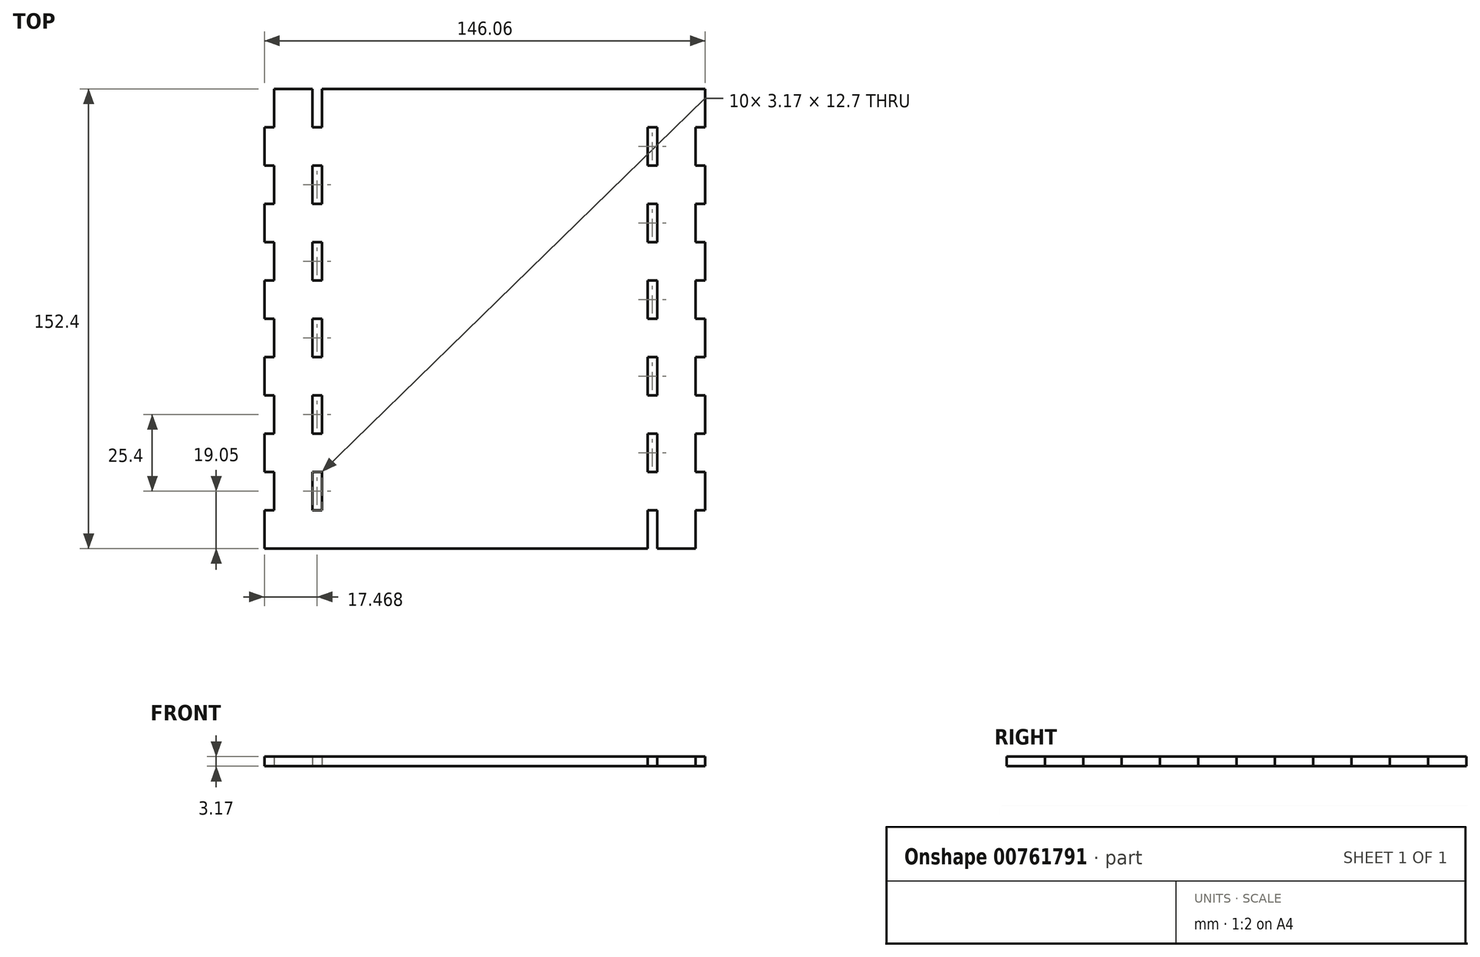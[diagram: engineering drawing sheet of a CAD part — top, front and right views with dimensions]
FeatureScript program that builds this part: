
annotation { "Feature Type Name" : "Feature", "Feature Type Description" : "" }
export const myFeature = defineFeature(function(context is Context, id is Id, definition is map)
    precondition{}
    {
        {
            var Q0;
            Q0=qCreatedBy(makeId("Top.planeOp"),FACE);
            var sketch = newSketch(context, id + "F0", { "sketchPlane" : qUnion([Q0])});
            skLineSegment(sketch, "E0.bottom", {"start": v(73.02, 76.2) * mm, "end": v(-73.03, 76.2) * mm});
            skLineSegment(sketch, "E0.top", {"start": v(73.03, -76.2) * mm, "end": v(-73.03, -76.2) * mm});
            skLineSegment(sketch, "E0.left", {"start": v(73.02, 76.2) * mm, "end": v(73.03, -76.2) * mm});
            skLineSegment(sketch, "E0.right", {"start": v(-73.03, 76.2) * mm, "end": v(-73.03, -76.2) * mm});
            skPoint(sketch, "E0.middle", {"position": v(0, 0) * mm});
            skLineSegment(sketch, "E1.bottom", {"start": v(-73.03, 76.2) * mm, "end": v(-69.85, 76.2) * mm});
            skLineSegment(sketch, "E1.top", {"start": v(-73.03, 63.5) * mm, "end": v(-69.85, 63.5) * mm});
            skLineSegment(sketch, "E1.left", {"start": v(-73.03, 76.2) * mm, "end": v(-73.03, 63.5) * mm});
            skLineSegment(sketch, "E1.right", {"start": v(-69.85, 76.2) * mm, "end": v(-69.85, 63.5) * mm});
            skLineSegment(sketch, "E2.0.1.0", {"start": v(-73.03, 50.8) * mm, "end": v(-69.85, 50.8) * mm});
            skLineSegment(sketch, "E2.0.1.1", {"start": v(-73.03, 50.8) * mm, "end": v(-73.03, 38.1) * mm});
            skLineSegment(sketch, "E2.0.1.2", {"start": v(-69.85, 50.8) * mm, "end": v(-69.85, 38.1) * mm});
            skLineSegment(sketch, "E2.0.1.3", {"start": v(-73.03, 38.1) * mm, "end": v(-69.85, 38.1) * mm});
            skLineSegment(sketch, "E2.0.2.0", {"start": v(-73.03, 25.4) * mm, "end": v(-69.85, 25.4) * mm});
            skLineSegment(sketch, "E2.0.2.1", {"start": v(-73.03, 25.4) * mm, "end": v(-73.03, 12.7) * mm});
            skLineSegment(sketch, "E2.0.2.2", {"start": v(-69.85, 25.4) * mm, "end": v(-69.85, 12.7) * mm});
            skLineSegment(sketch, "E2.0.2.3", {"start": v(-73.03, 12.7) * mm, "end": v(-69.85, 12.7) * mm});
            skLineSegment(sketch, "E2.0.3.0", {"start": v(-73.03, 0) * mm, "end": v(-69.85, 0) * mm});
            skLineSegment(sketch, "E2.0.3.1", {"start": v(-73.03, 0) * mm, "end": v(-73.03, -12.7) * mm});
            skLineSegment(sketch, "E2.0.3.2", {"start": v(-69.85, 0) * mm, "end": v(-69.85, -12.7) * mm});
            skLineSegment(sketch, "E2.0.3.3", {"start": v(-73.03, -12.7) * mm, "end": v(-69.85, -12.7) * mm});
            skLineSegment(sketch, "E2.0.4.0", {"start": v(-73.03, -25.4) * mm, "end": v(-69.85, -25.4) * mm});
            skLineSegment(sketch, "E2.0.4.1", {"start": v(-73.03, -25.4) * mm, "end": v(-73.03, -38.1) * mm});
            skLineSegment(sketch, "E2.0.4.2", {"start": v(-69.85, -25.4) * mm, "end": v(-69.85, -38.1) * mm});
            skLineSegment(sketch, "E2.0.4.3", {"start": v(-73.03, -38.1) * mm, "end": v(-69.85, -38.1) * mm});
            skLineSegment(sketch, "E2.0.5.0", {"start": v(-73.03, -50.8) * mm, "end": v(-69.85, -50.8) * mm});
            skLineSegment(sketch, "E2.0.5.1", {"start": v(-73.03, -50.8) * mm, "end": v(-73.03, -63.5) * mm});
            skLineSegment(sketch, "E2.0.5.2", {"start": v(-69.85, -50.8) * mm, "end": v(-69.85, -63.5) * mm});
            skLineSegment(sketch, "E2.0.5.3", {"start": v(-73.03, -63.5) * mm, "end": v(-69.85, -63.5) * mm});
            skLineSegment(sketch, "E2.1.0.0", {"start": v(-57.15, 76.2) * mm, "end": v(-53.98, 76.2) * mm});
            skLineSegment(sketch, "E2.1.0.1", {"start": v(-57.15, 76.2) * mm, "end": v(-57.15, 63.5) * mm});
            skLineSegment(sketch, "E2.1.0.2", {"start": v(-53.98, 76.2) * mm, "end": v(-53.98, 63.5) * mm});
            skLineSegment(sketch, "E2.1.0.3", {"start": v(-57.15, 63.5) * mm, "end": v(-53.98, 63.5) * mm});
            skLineSegment(sketch, "E2.1.1.0", {"start": v(-57.15, 50.8) * mm, "end": v(-53.98, 50.8) * mm});
            skLineSegment(sketch, "E2.1.1.1", {"start": v(-57.15, 50.8) * mm, "end": v(-57.15, 38.1) * mm});
            skLineSegment(sketch, "E2.1.1.2", {"start": v(-53.98, 50.8) * mm, "end": v(-53.98, 38.1) * mm});
            skLineSegment(sketch, "E2.1.1.3", {"start": v(-57.15, 38.1) * mm, "end": v(-53.98, 38.1) * mm});
            skLineSegment(sketch, "E2.1.2.0", {"start": v(-57.15, 25.4) * mm, "end": v(-53.98, 25.4) * mm});
            skLineSegment(sketch, "E2.1.2.1", {"start": v(-57.15, 25.4) * mm, "end": v(-57.15, 12.7) * mm});
            skLineSegment(sketch, "E2.1.2.2", {"start": v(-53.98, 25.4) * mm, "end": v(-53.98, 12.7) * mm});
            skLineSegment(sketch, "E2.1.2.3", {"start": v(-57.15, 12.7) * mm, "end": v(-53.98, 12.7) * mm});
            skLineSegment(sketch, "E2.1.3.0", {"start": v(-57.15, 0) * mm, "end": v(-53.98, 0) * mm});
            skLineSegment(sketch, "E2.1.3.1", {"start": v(-57.15, 0) * mm, "end": v(-57.15, -12.7) * mm});
            skLineSegment(sketch, "E2.1.3.2", {"start": v(-53.98, 0) * mm, "end": v(-53.98, -12.7) * mm});
            skLineSegment(sketch, "E2.1.3.3", {"start": v(-57.15, -12.7) * mm, "end": v(-53.98, -12.7) * mm});
            skLineSegment(sketch, "E2.1.4.0", {"start": v(-57.15, -25.4) * mm, "end": v(-53.98, -25.4) * mm});
            skLineSegment(sketch, "E2.1.4.1", {"start": v(-57.15, -25.4) * mm, "end": v(-57.15, -38.1) * mm});
            skLineSegment(sketch, "E2.1.4.2", {"start": v(-53.98, -25.4) * mm, "end": v(-53.98, -38.1) * mm});
            skLineSegment(sketch, "E2.1.4.3", {"start": v(-57.15, -38.1) * mm, "end": v(-53.98, -38.1) * mm});
            skLineSegment(sketch, "E2.1.5.0", {"start": v(-57.15, -50.8) * mm, "end": v(-53.98, -50.8) * mm});
            skLineSegment(sketch, "E2.1.5.1", {"start": v(-57.15, -50.8) * mm, "end": v(-57.15, -63.5) * mm});
            skLineSegment(sketch, "E2.1.5.2", {"start": v(-53.98, -50.8) * mm, "end": v(-53.98, -63.5) * mm});
            skLineSegment(sketch, "E2.1.5.3", {"start": v(-57.15, -63.5) * mm, "end": v(-53.98, -63.5) * mm});
            skLineSegment(sketch, "E2.direction1", {"start": v(-73.03, 76.2) * mm, "end": v(-57.15, 76.2) * mm, "construction": true});
            skLineSegment(sketch, "E2.direction2", {"start": v(-73.03, 76.2) * mm, "end": v(-73.03, 50.8) * mm, "construction": true});
            skLineSegment(sketch, "E3.bottom", {"start": v(73.03, -76.2) * mm, "end": v(69.85, -76.2) * mm});
            skLineSegment(sketch, "E3.top", {"start": v(73.02, -63.5) * mm, "end": v(69.85, -63.5) * mm});
            skLineSegment(sketch, "E3.left", {"start": v(73.03, -76.2) * mm, "end": v(73.03, -63.5) * mm});
            skLineSegment(sketch, "E3.right", {"start": v(69.85, -76.2) * mm, "end": v(69.85, -63.5) * mm});
            skLineSegment(sketch, "E4.0.1.0", {"start": v(73.03, -50.8) * mm, "end": v(69.85, -50.8) * mm});
            skLineSegment(sketch, "E4.0.1.1", {"start": v(69.85, -50.8) * mm, "end": v(69.85, -38.1) * mm});
            skLineSegment(sketch, "E4.0.1.2", {"start": v(73.02, -38.1) * mm, "end": v(69.85, -38.1) * mm});
            skLineSegment(sketch, "E4.0.1.3", {"start": v(73.03, -50.8) * mm, "end": v(73.03, -38.1) * mm});
            skLineSegment(sketch, "E4.0.2.0", {"start": v(73.03, -25.4) * mm, "end": v(69.85, -25.4) * mm});
            skLineSegment(sketch, "E4.0.2.1", {"start": v(69.85, -25.4) * mm, "end": v(69.85, -12.7) * mm});
            skLineSegment(sketch, "E4.0.2.2", {"start": v(73.02, -12.7) * mm, "end": v(69.85, -12.7) * mm});
            skLineSegment(sketch, "E4.0.2.3", {"start": v(73.03, -25.4) * mm, "end": v(73.03, -12.7) * mm});
            skLineSegment(sketch, "E4.0.3.0", {"start": v(73.03, 0) * mm, "end": v(69.85, 0) * mm});
            skLineSegment(sketch, "E4.0.3.1", {"start": v(69.85, 0) * mm, "end": v(69.85, 12.7) * mm});
            skLineSegment(sketch, "E4.0.3.2", {"start": v(73.02, 12.7) * mm, "end": v(69.85, 12.7) * mm});
            skLineSegment(sketch, "E4.0.3.3", {"start": v(73.03, 0) * mm, "end": v(73.03, 12.7) * mm});
            skLineSegment(sketch, "E4.0.4.0", {"start": v(73.03, 25.4) * mm, "end": v(69.85, 25.4) * mm});
            skLineSegment(sketch, "E4.0.4.1", {"start": v(69.85, 25.4) * mm, "end": v(69.85, 38.1) * mm});
            skLineSegment(sketch, "E4.0.4.2", {"start": v(73.02, 38.1) * mm, "end": v(69.85, 38.1) * mm});
            skLineSegment(sketch, "E4.0.4.3", {"start": v(73.03, 25.4) * mm, "end": v(73.03, 38.1) * mm});
            skLineSegment(sketch, "E4.0.5.0", {"start": v(73.03, 50.8) * mm, "end": v(69.85, 50.8) * mm});
            skLineSegment(sketch, "E4.0.5.1", {"start": v(69.85, 50.8) * mm, "end": v(69.85, 63.5) * mm});
            skLineSegment(sketch, "E4.0.5.2", {"start": v(73.02, 63.5) * mm, "end": v(69.85, 63.5) * mm});
            skLineSegment(sketch, "E4.0.5.3", {"start": v(73.03, 50.8) * mm, "end": v(73.03, 63.5) * mm});
            skLineSegment(sketch, "E4.1.0.0", {"start": v(57.15, -76.2) * mm, "end": v(53.97, -76.2) * mm});
            skLineSegment(sketch, "E4.1.0.1", {"start": v(53.97, -76.2) * mm, "end": v(53.97, -63.5) * mm});
            skLineSegment(sketch, "E4.1.0.2", {"start": v(57.15, -63.5) * mm, "end": v(53.97, -63.5) * mm});
            skLineSegment(sketch, "E4.1.0.3", {"start": v(57.15, -76.2) * mm, "end": v(57.15, -63.5) * mm});
            skLineSegment(sketch, "E4.1.1.0", {"start": v(57.15, -50.8) * mm, "end": v(53.97, -50.8) * mm});
            skLineSegment(sketch, "E4.1.1.1", {"start": v(53.97, -50.8) * mm, "end": v(53.97, -38.1) * mm});
            skLineSegment(sketch, "E4.1.1.2", {"start": v(57.15, -38.1) * mm, "end": v(53.97, -38.1) * mm});
            skLineSegment(sketch, "E4.1.1.3", {"start": v(57.15, -50.8) * mm, "end": v(57.15, -38.1) * mm});
            skLineSegment(sketch, "E4.1.2.0", {"start": v(57.15, -25.4) * mm, "end": v(53.97, -25.4) * mm});
            skLineSegment(sketch, "E4.1.2.1", {"start": v(53.97, -25.4) * mm, "end": v(53.97, -12.7) * mm});
            skLineSegment(sketch, "E4.1.2.2", {"start": v(57.15, -12.7) * mm, "end": v(53.97, -12.7) * mm});
            skLineSegment(sketch, "E4.1.2.3", {"start": v(57.15, -25.4) * mm, "end": v(57.15, -12.7) * mm});
            skLineSegment(sketch, "E4.1.3.0", {"start": v(57.15, 0) * mm, "end": v(53.97, 0) * mm});
            skLineSegment(sketch, "E4.1.3.1", {"start": v(53.97, 0) * mm, "end": v(53.97, 12.7) * mm});
            skLineSegment(sketch, "E4.1.3.2", {"start": v(57.15, 12.7) * mm, "end": v(53.97, 12.7) * mm});
            skLineSegment(sketch, "E4.1.3.3", {"start": v(57.15, 0) * mm, "end": v(57.15, 12.7) * mm});
            skLineSegment(sketch, "E4.1.4.0", {"start": v(57.15, 25.4) * mm, "end": v(53.97, 25.4) * mm});
            skLineSegment(sketch, "E4.1.4.1", {"start": v(53.97, 25.4) * mm, "end": v(53.97, 38.1) * mm});
            skLineSegment(sketch, "E4.1.4.2", {"start": v(57.15, 38.1) * mm, "end": v(53.97, 38.1) * mm});
            skLineSegment(sketch, "E4.1.4.3", {"start": v(57.15, 25.4) * mm, "end": v(57.15, 38.1) * mm});
            skLineSegment(sketch, "E4.1.5.0", {"start": v(57.15, 50.8) * mm, "end": v(53.97, 50.8) * mm});
            skLineSegment(sketch, "E4.1.5.1", {"start": v(53.97, 50.8) * mm, "end": v(53.97, 63.5) * mm});
            skLineSegment(sketch, "E4.1.5.2", {"start": v(57.15, 63.5) * mm, "end": v(53.97, 63.5) * mm});
            skLineSegment(sketch, "E4.1.5.3", {"start": v(57.15, 50.8) * mm, "end": v(57.15, 63.5) * mm});
            skLineSegment(sketch, "E4.direction1", {"start": v(69.85, -76.2) * mm, "end": v(53.97, -76.2) * mm, "construction": true});
            skLineSegment(sketch, "E4.direction2", {"start": v(69.85, -76.2) * mm, "end": v(69.85, -50.8) * mm, "construction": true});
            skSolve(sketch);
        }
        {
            var Q0;
            {var subQ39=sQuery(id+"F0.wireOp",EDGE,"E1.top");Q0=makeQuery(id+"F0.imprint","IMPRINT",FACE,{"disambiguationData":[TD([[makeQuery(id+"F0.imprint","IMPRINT",EDGE,{"derivedFrom":subQ39}),-1.0]])]});}
            extrude(context, id + "F1", {"entities" : qUnion([Q0]), "depth" : 3.17 * mm, "offsetDistance" : 25.4 * mm});
        }
    });
